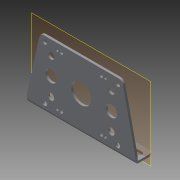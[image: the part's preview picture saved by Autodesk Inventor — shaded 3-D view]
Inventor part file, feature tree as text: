
AUTODESK INVENTOR PART (.ipt)
format: ipt  version: 2015 SP1 (Build 190203100, 203)  size: 137,216 bytes
history: native  units: in
note: dims shown in document units (in); Inventor stores cm internally (conversion verified against a paired STEP export)
features: other x2, plane x1, imported_body x1
ambient origin geometry x8: Origin, YZ Plane, XZ Plane, XY Plane, X Axis, Y Axis, Z Axis, Center Point
bodies: Body1 (feature_tree)
feature tree (4):
  other  "Single_d02"
  other  "Single_d02.ipt1"
  plane  "Work Plane1"
  imported_body  "Base1"
